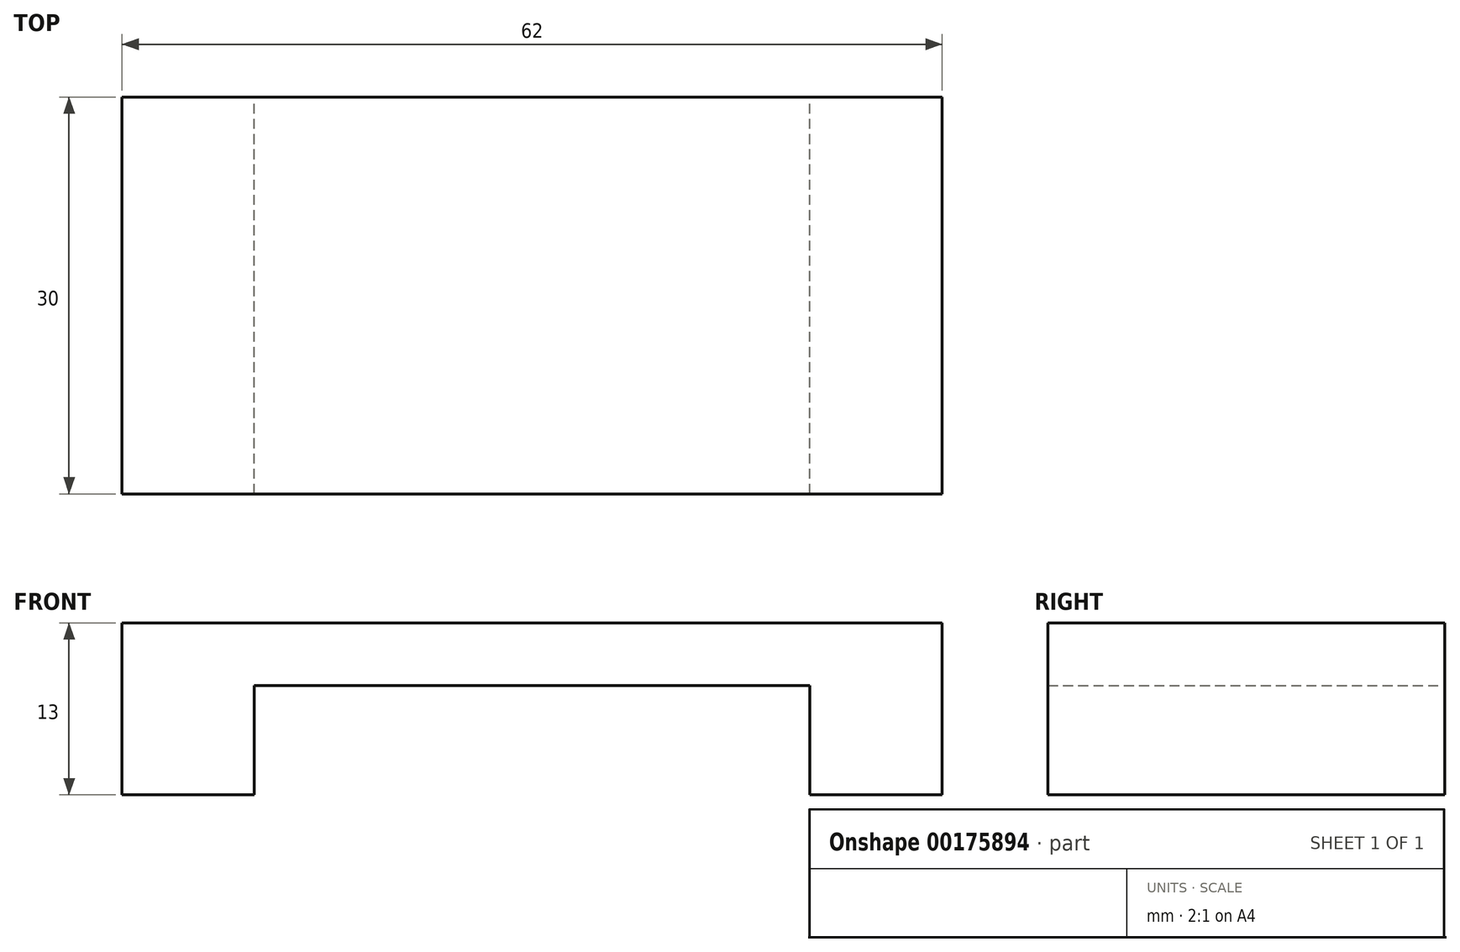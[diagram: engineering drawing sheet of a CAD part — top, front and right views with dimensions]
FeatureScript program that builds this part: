
annotation { "Feature Type Name" : "Feature", "Feature Type Description" : "" }
export const myFeature = defineFeature(function(context is Context, id is Id, definition is map)
    precondition{}
    {
        {
            var Q0;
            Q0=qCreatedBy(makeId("Front.planeOp"),FACE);
            var sketch = newSketch(context, id + "F0", { "sketchPlane" : qUnion([Q0])});
            skLineSegment(sketch, "E0", {"start": v(0, 0) * mm, "end": v(62, 0) * mm});
            skLineSegment(sketch, "E1", {"start": v(0, 0) * mm, "end": v(0, -13) * mm});
            skLineSegment(sketch, "E2", {"start": v(0, -13) * mm, "end": v(10, -13) * mm});
            skLineSegment(sketch, "E3", {"start": v(10, -13) * mm, "end": v(10, -10.18) * mm});
            skLineSegment(sketch, "E4", {"start": v(52, -10.18) * mm, "end": v(52, -13) * mm});
            skLineSegment(sketch, "E5", {"start": v(52, -13) * mm, "end": v(62, -13) * mm});
            skLineSegment(sketch, "E6", {"start": v(62, 0) * mm, "end": v(62, -13) * mm});
            skLineSegment(sketch, "E7", {"start": v(10, -10.18) * mm, "end": v(10, -4.73) * mm});
            skLineSegment(sketch, "E8", {"start": v(10, -4.73) * mm, "end": v(52, -4.73) * mm});
            skLineSegment(sketch, "E9", {"start": v(52, -4.73) * mm, "end": v(52, -10.18) * mm});
            skSolve(sketch);
        }
        {
            var Q0;
            Q0 = qSketchRegion(id + "F0", true);
            extrude(context, id + "F1", {"entities" : qUnion([Q0]), "depth" : 30 * mm});
        }
    });
